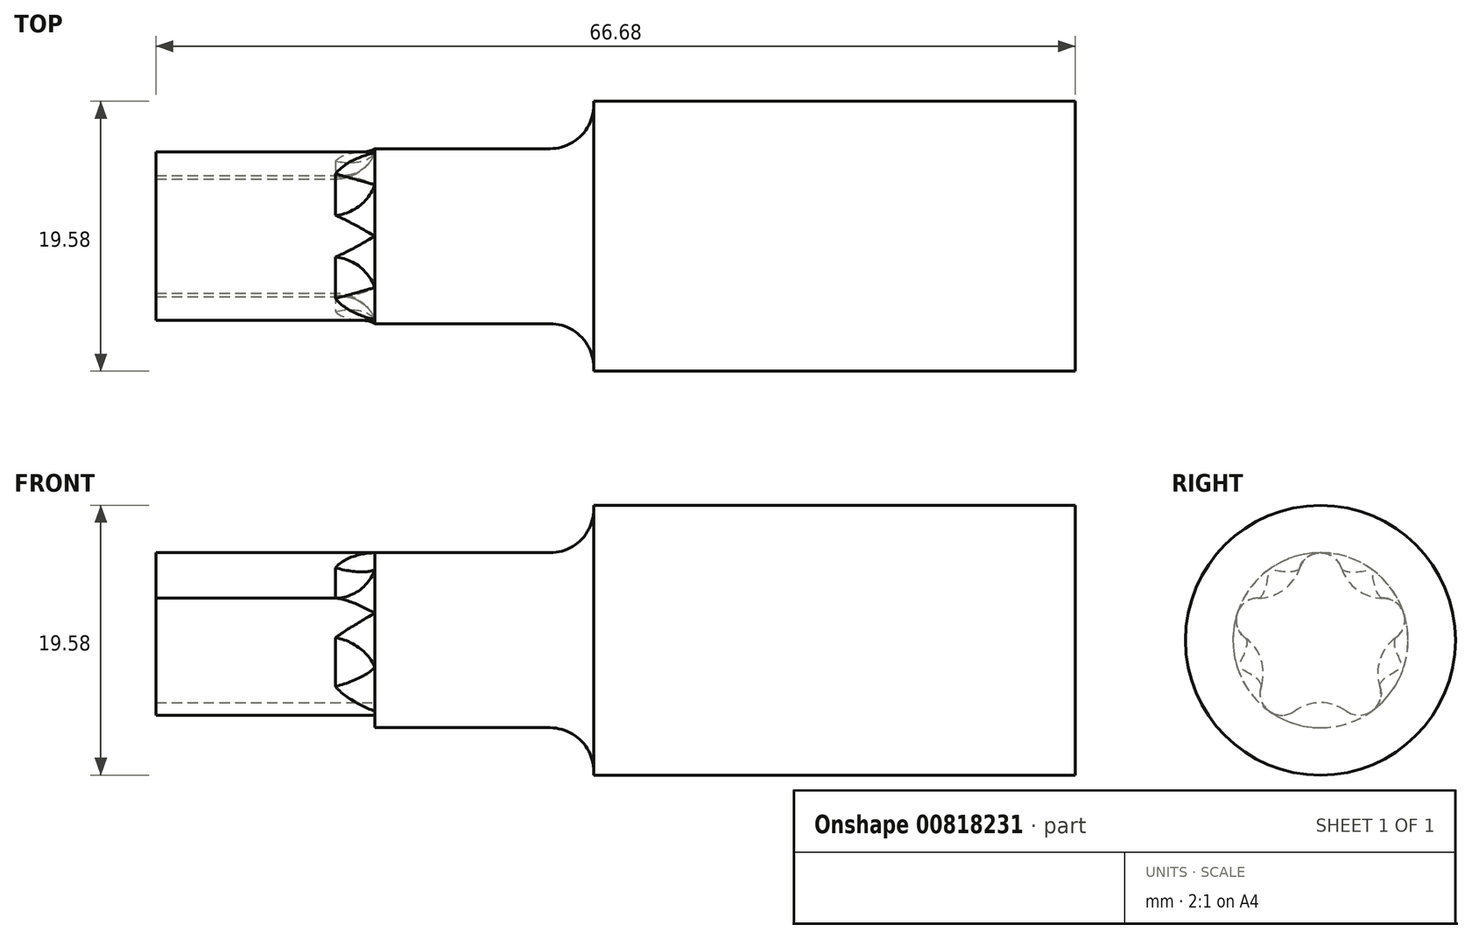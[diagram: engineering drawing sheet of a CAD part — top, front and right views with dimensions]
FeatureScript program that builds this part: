
annotation { "Feature Type Name" : "Feature", "Feature Type Description" : "" }
export const myFeature = defineFeature(function(context is Context, id is Id, definition is map)
    precondition{}
    {
        {
            var Q0;
            Q0=qCreatedBy(makeId("Front.planeOp"),FACE);
            var sketch = newSketch(context, id + "F0", { "sketchPlane" : qUnion([Q0])});
            skLineSegment(sketch, "E0", {"start": v(0, 0) * mm, "end": v(0, 6.35) * mm});
            skLineSegment(sketch, "E1", {"start": v(0, 6.35) * mm, "end": v(15.87, 6.35) * mm});
            skLineSegment(sketch, "E2", {"start": v(15.88, 6.35) * mm, "end": v(15.88, 9.8) * mm});
            skLineSegment(sketch, "E3", {"start": v(15.88, 9.8) * mm, "end": v(50.8, 9.8) * mm});
            skLineSegment(sketch, "E4", {"start": v(50.8, 9.8) * mm, "end": v(50.8, 0) * mm});
            skLineSegment(sketch, "E5", {"start": v(50.8, 0) * mm, "end": v(0, 0) * mm});
            skLineSegment(sketch, "E6", {"start": v(0, 0) * mm, "end": v(0, -6.7) * mm, "construction": true});
            skLineSegment(sketch, "E7", {"start": v(0, 0) * mm, "end": v(-12.52, 0) * mm, "construction": true});
            skSolve(sketch);
        }
        {
            var Q0;
            Q0 = qSketchRegion(id + "F0", true);
            var Q1;
            Q1=sQuery(id+"F0.wireOp",EDGE,"E7");
            revolve(context, id + "F1", {"surfaceOperationType" : NewSurfaceOperationType.NEW, "entities" : qUnion([Q0]), "axis" : qUnion([Q1]), "revolveType" : RevolveType.FULL});
        }
        {
            var Q0;
            Q0=makeQuery(id+"F1.opRevolve","SWEPT_EDGE",EDGE,{"disambiguationData":[OSD([sQuery(id+"F0.wireOp",EDGE,"E1"),sQuery(id+"F0.wireOp",EDGE,"E2")])]});
            fillet(context, id + "F2", {"entities" : qUnion([Q0]), "radius" : 3.17 * mm, "tangentPropagation" : true, "allowEdgeOverflow" : false});
        }
        {
            var Q0;
            Q0=makeQuery(id+"F1.opRevolve","SWEPT_FACE",FACE,{"disambiguationData":[OSD([sQuery(id+"F0.wireOp",EDGE,"E0")])]});
            var sketch = newSketch(context, id + "F3", { "sketchPlane" : qUnion([Q0])});
            skArc(sketch, "E8", {"start": v(1.5, 5.25) * mm, "mid": v(0, 6.35) * mm, "end": v(-1.5, 5.25) * mm});
            skArc(sketch, "E9", {"start": v(1.5, 5.25) * mm, "mid": v(2.66, 3.67) * mm, "end": v(4.53, 3.06) * mm});
            skArc(sketch, "E10.1.0", {"start": v(-4.53, 3.06) * mm, "mid": v(-6.04, 1.96) * mm, "end": v(-5.46, 0.19) * mm});
            skArc(sketch, "E10.2.0", {"start": v(-4.3, -3.36) * mm, "mid": v(-3.73, -5.14) * mm, "end": v(-1.87, -5.14) * mm});
            skArc(sketch, "E10.3.0", {"start": v(1.87, -5.14) * mm, "mid": v(3.73, -5.14) * mm, "end": v(4.3, -3.36) * mm});
            skArc(sketch, "E10.4.0", {"start": v(5.46, 0.19) * mm, "mid": v(6.04, 1.96) * mm, "end": v(4.53, 3.06) * mm});
            skPoint(sketch, "E10.center", {"position": v(0, 0) * mm});
            skArc(sketch, "E11.1.0", {"start": v(-4.53, 3.06) * mm, "mid": v(-2.66, 3.67) * mm, "end": v(-1.5, 5.25) * mm});
            skArc(sketch, "E11.2.0", {"start": v(-4.3, -3.36) * mm, "mid": v(-4.3, -1.4) * mm, "end": v(-5.46, 0.19) * mm});
            skArc(sketch, "E11.3.0", {"start": v(1.87, -5.14) * mm, "mid": v(0, -4.53) * mm, "end": v(-1.87, -5.14) * mm});
            skArc(sketch, "E11.4.0", {"start": v(5.46, 0.19) * mm, "mid": v(4.3, -1.4) * mm, "end": v(4.3, -3.36) * mm});
            skSolve(sketch);
        }
        {
            var Q0;
            Q0 = qSketchRegion(id + "F3", true);
            extrude(context, id + "F4", {"entities" : qUnion([Q0]), "operationType" : NewBodyOperationType.ADD, "depth" : 15.88 * mm, "offsetDistance" : 25.4 * mm});
        }
        {
            var Q0;
            Q0=makeQuery(id+"F4.opExtrude","CAP_EDGE",EDGE,{"disambiguationData":[OSD([sQuery(id+"F3.wireOp",EDGE,"E11.1.0")])],"isStart":true});
            var Q1;
            Q1=makeQuery(id+"F4.opExtrude","CAP_EDGE",EDGE,{"disambiguationData":[OSD([sQuery(id+"F3.wireOp",EDGE,"E9")])],"isStart":true});
            var Q2;
            Q2=makeQuery(id+"F4.opExtrude","CAP_EDGE",EDGE,{"disambiguationData":[OSD([sQuery(id+"F3.wireOp",EDGE,"E11.4.0")])],"isStart":true});
            var Q3;
            Q3=makeQuery(id+"F4.opExtrude","CAP_EDGE",EDGE,{"disambiguationData":[OSD([sQuery(id+"F3.wireOp",EDGE,"E11.3.0")])],"isStart":true});
            var Q4;
            Q4=makeQuery(id+"F4.opExtrude","CAP_EDGE",EDGE,{"disambiguationData":[OSD([sQuery(id+"F3.wireOp",EDGE,"E11.2.0")])],"isStart":true});
            fillet(context, id + "F5", {"entities" : qUnion([Q0, Q1, Q2, Q3, Q4]), "radius" : 3.17 * mm, "allowEdgeOverflow" : false});
        }
    });
